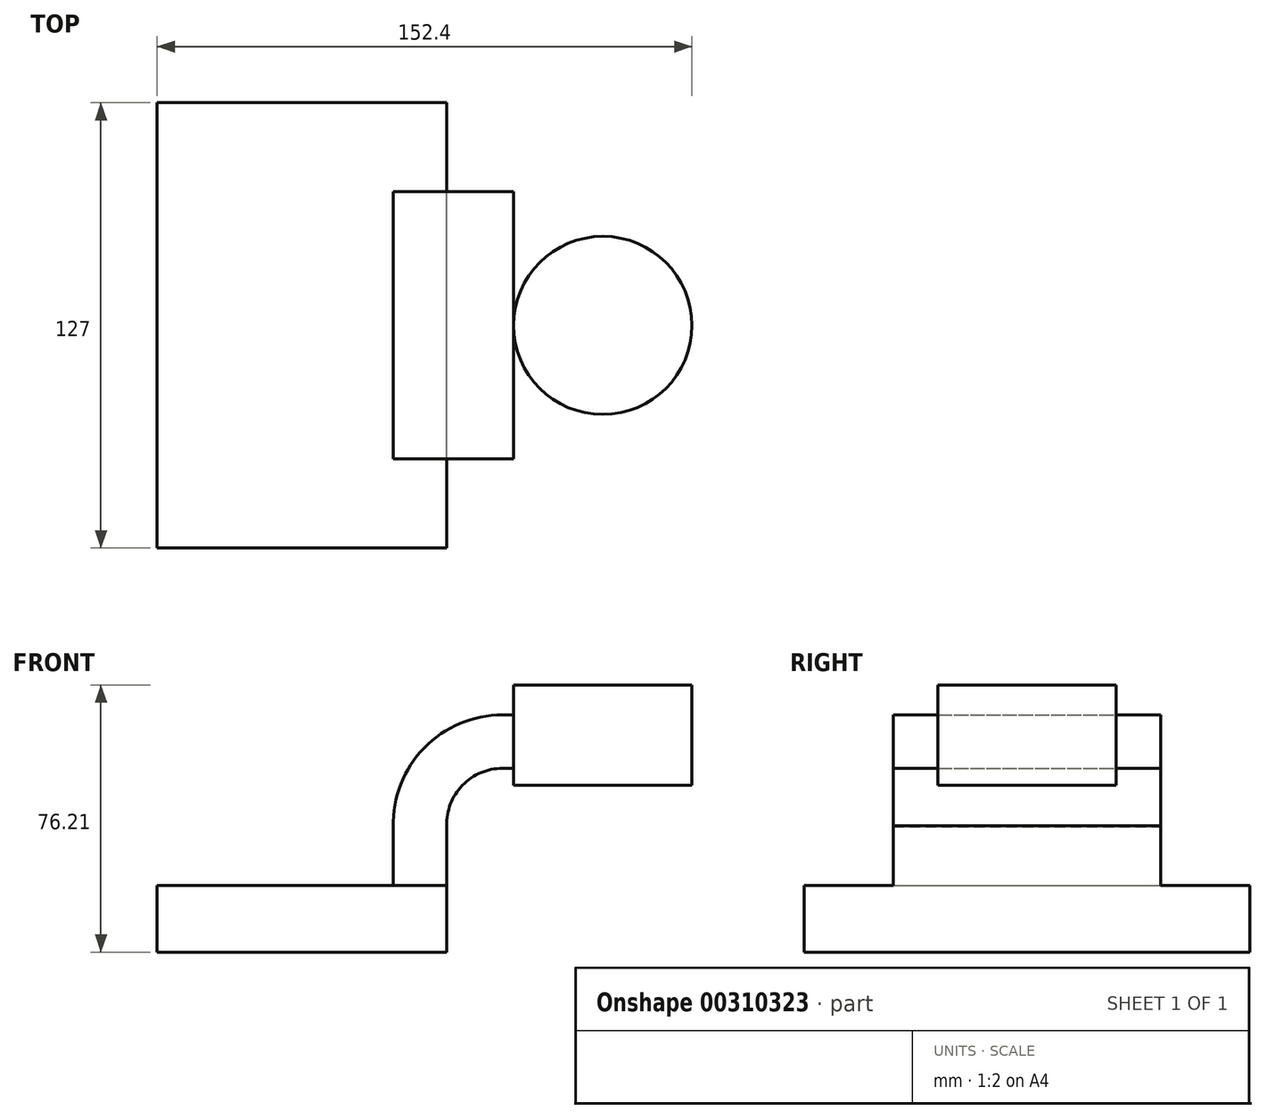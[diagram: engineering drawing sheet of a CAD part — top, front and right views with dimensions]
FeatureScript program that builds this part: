
annotation { "Feature Type Name" : "Feature", "Feature Type Description" : "" }
export const myFeature = defineFeature(function(context is Context, id is Id, definition is map)
    precondition{}
    {
        {
            var Q0;
            Q0=qCreatedBy(makeId("Front.planeOp"),FACE);
            var sketch = newSketch(context, id + "F0", { "sketchPlane" : qUnion([Q0])});
            skLineSegment(sketch, "E0.bottom", {"start": v(41.27, 9.53) * mm, "end": v(-41.28, 9.53) * mm});
            skLineSegment(sketch, "E0.top", {"start": v(41.28, -9.52) * mm, "end": v(-41.28, -9.52) * mm});
            skLineSegment(sketch, "E0.left", {"start": v(41.28, 9.53) * mm, "end": v(41.28, -9.52) * mm});
            skLineSegment(sketch, "E0.right", {"start": v(-41.28, 9.53) * mm, "end": v(-41.28, -9.52) * mm});
            skPoint(sketch, "E0.middle", {"position": v(0, 0) * mm});
            skLineSegment(sketch, "E1.bottom", {"start": v(47.58, -2812.67) * mm, "end": v(98.38, -2812.67) * mm});
            skLineSegment(sketch, "E1.top", {"start": v(47.58, -2784.1) * mm, "end": v(98.38, -2784.1) * mm});
            skLineSegment(sketch, "E1.left", {"start": v(47.58, -2812.67) * mm, "end": v(47.58, -2784.1) * mm});
            skLineSegment(sketch, "E1.right", {"start": v(98.38, -2812.67) * mm, "end": v(98.38, -2784.1) * mm});
            skPoint(sketch, "E1.middle", {"position": v(72.98, -2798.38) * mm});
            skArc(sketch, "E2", {"start": v(72.98, -2798.38) * mm, "mid": v(57.75, -2781.37) * mm, "end": v(41.27, -2797.19) * mm});
            skLineSegment(sketch, "E3", {"start": v(41.27, 9.53) * mm, "end": v(41.27, 26.43) * mm});
            skLineSegment(sketch, "E4.bottom", {"start": v(111.12, 66.68) * mm, "end": v(60.32, 66.68) * mm});
            skLineSegment(sketch, "E4.top", {"start": v(111.12, 38.1) * mm, "end": v(60.32, 38.1) * mm});
            skLineSegment(sketch, "E4.left", {"start": v(111.12, 66.68) * mm, "end": v(111.12, 38.1) * mm});
            skLineSegment(sketch, "E4.right", {"start": v(60.32, 66.68) * mm, "end": v(60.32, 38.1) * mm});
            skPoint(sketch, "E4.middle", {"position": v(85.72, 52.39) * mm});
            skLineSegment(sketch, "E5", {"start": v(57.14, 42.88) * mm, "end": v(85.55, 42.88) * mm});
            skArc(sketch, "E6", {"start": v(57.14, 42.88) * mm, "mid": v(45.72, 38.02) * mm, "end": v(41.28, 26.43) * mm});
            skLineSegment(sketch, "E7.0", {"start": v(26.03, 9.53) * mm, "end": v(26.03, 26.2) * mm});
            skArc(sketch, "E7.1", {"start": v(57.14, 58.12) * mm, "mid": v(34.86, 48.72) * mm, "end": v(26.03, 26.2) * mm});
            skLineSegment(sketch, "E7.2", {"start": v(57.14, 58.12) * mm, "end": v(85.55, 58.12) * mm});
            skFitSpline(sketch, "E8", {"points": [v(-41.28, 9.53) * mm, v(-11.8, 55.47) * mm, v(60.32, 66.67) * mm], "startDerivative": vector(1.6, 174.95) * mm, "endDerivative": vector(268.4, 2.68) * mm});
            skLineSegment(sketch, "E9", {"start": v(85.72, 38.1) * mm, "end": v(85.72, 66.68) * mm});
            skSolve(sketch);
        }
        {
            var Q0;
            Q0=makeQuery(id+"F0.imprint","IMPRINT",FACE,{"disambiguationData":[TD([[makeQuery(id+"F0.imprint","IMPRINT",EDGE,{"derivedFrom":sQuery(id+"F0.wireOp",EDGE,"E0.top")}),-1.0]])]});
            extrude(context, id + "F1", {"entities" : qUnion([Q0]), "endBound" : BoundingType.SYMMETRIC, "depth" : 127 * mm});
        }
        {
            var Q0;
            {var subQ6=sQuery(id+"F0.wireOp",EDGE,"E3");Q0=makeQuery(id+"F0.imprint","IMPRINT",FACE,{"disambiguationData":[TD([[makeQuery(id+"F0.imprint","IMPRINT",EDGE,{"derivedFrom":subQ6}),1.0]])]});}
            extrude(context, id + "F2", {"entities" : qUnion([Q0]), "operationType" : NewBodyOperationType.ADD, "endBound" : BoundingType.SYMMETRIC, "depth" : 76.2 * mm});
        }
        {
            var Q0;
            {var subQ0=sQuery(id+"F0.wireOp",EDGE,"E4.left");Q0=makeQuery(id+"F0.imprint","IMPRINT",FACE,{"disambiguationData":[TD([[makeQuery(id+"F0.imprint","IMPRINT",EDGE,{"derivedFrom":subQ0}),-1.0]])]});}
            var Q1;
            Q1=sQuery(id+"F0.wireOp",EDGE,"E9");
            revolve(context, id + "F3", {"operationType" : NewBodyOperationType.ADD, "entities" : qUnion([Q0]), "axis" : qUnion([Q1]), "revolveType" : RevolveType.FULL});
        }
    });
